# Revit family: Basin-Undercounter-American_Standard-Edgemere-0545.000
name_source: partatom
category: Plumbing Fixtures
revit_build: Autodesk Revit 2018 (Build: 20170223_1515(x64)
units: mm (PartAtom-declared; Revit-internal decimal feet)

## family parameters
Always vertical = No
Cut with Voids When Loaded = Yes
OmniClass Number = 23.45.05.14.14
OmniClass Title = Sinks/Lavatories
Part Type = Normal
Room Calculation Point = No
Round Connector Dimension = Use Diameter
Shared = Yes
Work Plane-Based = Yes

## types (1)
- 0545.000
    ADA Compliant = Yes
    Assembly Code = D2010310
    Basin Shape = Rectangular
    CW Connection = Yes
    CWFU = 1.5
    Cold Water Connection Diameter = 3/8"
    Cold Water Connection Height = 23 1/2"
    Cold Water Connection Width = 4"
    Default Elevation = 34"
    Description = The Edgemere Rectangle Bathroom Sink is an undermount sink made from durable vitreous china that will fit perfectly under the bathroom counter. Designed with a front overflow, this exceptional bathroom sink coordinates perfectly with the full Edgemere Suite of bathroom fixtures and fittings. It includes a mounting kit and template, for easy installation.
    Finish = Vitreous China-American Standard-020-White
    HW Connection = Yes
    HWFU = 1.5
    Height = 5 1/4"
    Hot Water Connection Diameter = 0"
    Hot Water Connection Height = 23 1/2"
    Hot Water Connection Width = 4"
    IAPMO Compliance = ASME A112.19.2/CSA B45.1
    Installation Type = Undermount
    Length = 16 1/8"
    Manufacturer = American Standard
    Material = Vitreous China-American Standard-020-White
    Model = 0545.000
    Price = Prices may vary. Please consult Manufacturer Representative for most up-to-date price list.
    Product Documentation Link = https://americanstandard.box.com
    Product Page URL = https://www.americanstandard-us.com
    Revised Date = 09/23/2021
    URL = https://www.americanstandard-us.com
    Vent Connection = No
    WFU = 2
    Warranty Information = One Year Limited Warranty
    Waste Connection = Yes
    Waste Connection Diameter = 1 1/4"
    Waste Connection Height = 21"
    Width = 18 1/2"

## geometry (parser evidence)
native form markers: Sweep x2
no freeform markers — native parametric forms only
